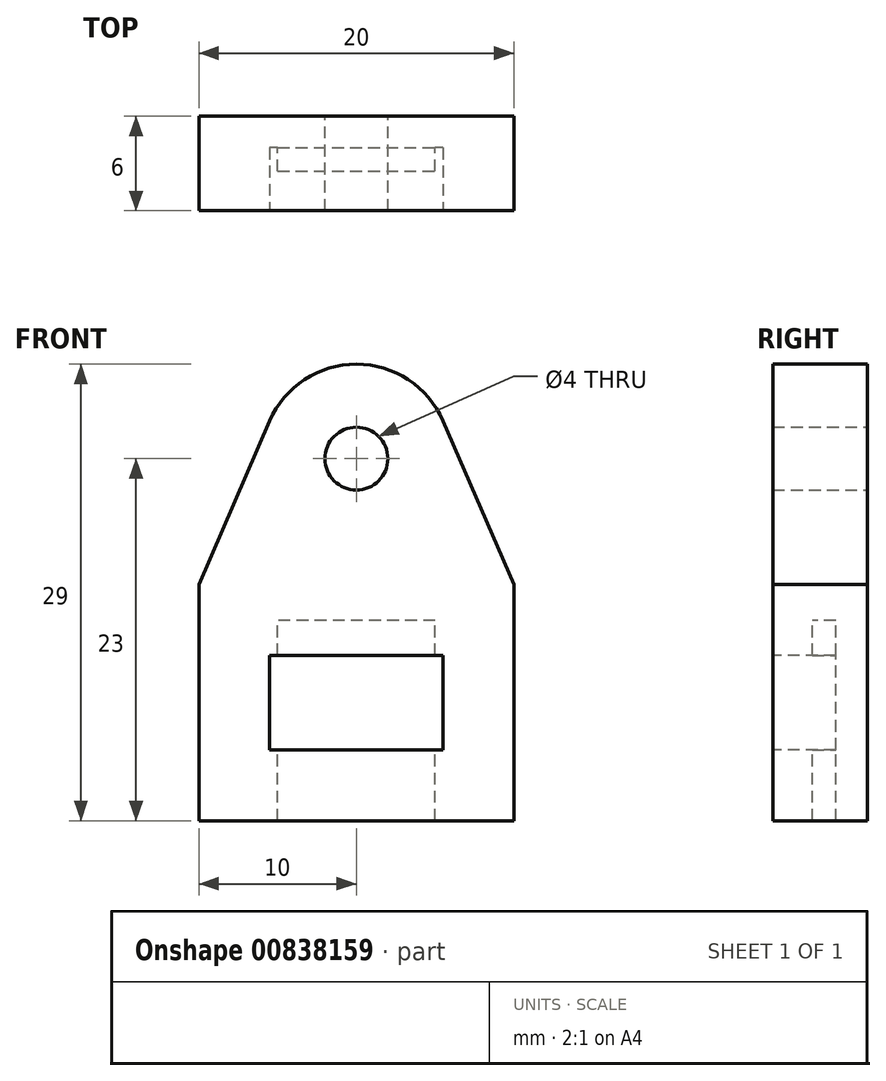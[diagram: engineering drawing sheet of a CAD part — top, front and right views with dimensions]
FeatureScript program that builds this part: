
annotation { "Feature Type Name" : "Feature", "Feature Type Description" : "" }
export const myFeature = defineFeature(function(context is Context, id is Id, definition is map)
    precondition{}
    {
        {
            var Q0;
            Q0=qCreatedBy(makeId("Front.planeOp"),FACE);
            var sketch = newSketch(context, id + "F0", { "sketchPlane" : qUnion([Q0])});
            skLineSegment(sketch, "E0.bottom", {"start": v(0, 0) * mm, "end": v(-20, 0) * mm});
            skLineSegment(sketch, "E0.top", {"start": v(0, 15) * mm, "end": v(-20, 15) * mm});
            skLineSegment(sketch, "E0.left", {"start": v(0, 0) * mm, "end": v(0, 15) * mm});
            skLineSegment(sketch, "E0.right", {"start": v(-20, 0) * mm, "end": v(-20, 15) * mm});
            skLineSegment(sketch, "E1", {"start": v(-10, 43.29) * mm, "end": v(-10, -25.8) * mm, "construction": true});
            skPoint(sketch, "E1.startSnap0", {"position": v(-10, 15) * mm});
            skPoint(sketch, "E1.endSnap0", {"position": v(-10, 0) * mm});
            skPoint(sketch, "E2", {"position": v(-10, 23) * mm});
            skCircle(sketch, "E3", {"center": v(-10, 23) * mm, "radius": 6 * mm});
            skLineSegment(sketch, "E4", {"start": v(-20, 15) * mm, "end": v(-15.5, 25.38) * mm});
            skLineSegment(sketch, "E5", {"start": v(0, 15) * mm, "end": v(-4.5, 25.38) * mm});
            skCircle(sketch, "E6.0", {"center": v(-10, 23) * mm, "radius": 2 * mm});
            skLineSegment(sketch, "E7", {"start": v(-23.7, 7.5) * mm, "end": v(3.2, 7.5) * mm, "construction": true});
            skPoint(sketch, "E7.startSnap0", {"position": v(-20, 7.5) * mm});
            skPoint(sketch, "E8", {"position": v(-10, 7.5) * mm});
            skPoint(sketch, "E8.positionSnap0", {"position": v(-10, 8.74) * mm});
            skLineSegment(sketch, "E9.bottom", {"start": v(-5, 5) * mm, "end": v(-15, 5) * mm});
            skLineSegment(sketch, "E9.top", {"start": v(-5, 10) * mm, "end": v(-15, 10) * mm});
            skLineSegment(sketch, "E9.left", {"start": v(-5, 5) * mm, "end": v(-5, 10) * mm});
            skLineSegment(sketch, "E9.right", {"start": v(-15, 5) * mm, "end": v(-15, 10) * mm});
            skLineSegment(sketch, "E10.bottom", {"start": v(-18, 0) * mm, "end": v(-2, 0) * mm});
            skLineSegment(sketch, "E10.top", {"start": v(-18, 12.72) * mm, "end": v(-2, 12.72) * mm});
            skLineSegment(sketch, "E10.left", {"start": v(-18, 0) * mm, "end": v(-18, 12.72) * mm});
            skLineSegment(sketch, "E10.right", {"start": v(-2, 0) * mm, "end": v(-2, 12.72) * mm});
            skLineSegment(sketch, "E11", {"start": v(-20, 0) * mm, "end": v(-18, 0) * mm});
            skLineSegment(sketch, "E12", {"start": v(-2, 0) * mm, "end": v(0, 0) * mm});
            skSolve(sketch);
        }
        {
            var Q0;
            Q0=makeQuery(id+"F0.imprint","IMPRINT",FACE,{"disambiguationData":[TD([[makeQuery(id+"F0.imprint","IMPRINT",EDGE,{"derivedFrom":sQuery(id+"F0.wireOp",EDGE,"E6.0")}),-1.0]])]});
            var Q1;
            Q1=makeQuery(id+"F0.imprint","IMPRINT",FACE,{"disambiguationData":[TD([[makeQuery(id+"F0.imprint","IMPRINT",EDGE,{"derivedFrom":sQuery(id+"F0.wireOp",EDGE,"E0.top")}),-1.0]])]});
            var Q2;
            Q2=makeQuery(id+"F0.imprint","IMPRINT",FACE,{"disambiguationData":[TD([[makeQuery(id+"F0.imprint","IMPRINT",EDGE,{"derivedFrom":sQuery(id+"F0.wireOp",EDGE,"E0.top")}),1.0]])]});
            var Q3;
            Q3=makeQuery(id+"F0.imprint","IMPRINT",FACE,{"disambiguationData":[TD([[makeQuery(id+"F0.imprint","IMPRINT",EDGE,{"derivedFrom":sQuery(id+"F0.wireOp",EDGE,"E9.bottom")}),1.0]])]});
            var Q4;
            Q4=makeQuery(id+"F0.imprint","IMPRINT",FACE,{"disambiguationData":[TD([[makeQuery(id+"F0.imprint","IMPRINT",EDGE,{"derivedFrom":sQuery(id+"F0.wireOp",EDGE,"E9.bottom")}),-1.0]])]});
            extrude(context, id + "F1", {"entities" : qUnion([Q0, Q1, Q2, Q3, Q4]), "depth" : 6 * mm, "offsetDistance" : 25 * mm});
        }
        {
            var Q0;
            Q0=sQuery(id+"F0.wireOp",EDGE,"E10.top");
            var Q1;
            Q1=qCreatedBy(makeId("Top.planeOp"),FACE);
            cPlane(context, id + "F2", {"entities" : qUnion([Q0, Q1]), "cplaneType" : CPlaneType.LINE_ANGLE, "offset" : 25 * mm, "angle" : 0 * degree, "width" : 150 * mm, "height" : 150 * mm});
        }
        {
            var Q0;
            Q0=qCreatedBy(id+"F2.planeOp",FACE);
            var sketch = newSketch(context, id + "F3", { "sketchPlane" : qUnion([Q0])});
            skPoint(sketch, "E13.0", {"position": v(-10, 0) * mm});
            skLineSegment(sketch, "E14", {"start": v(-10, 6.29) * mm, "end": v(-10, -2.33) * mm, "construction": true});
            skPoint(sketch, "E15", {"position": v(-10, 2.75) * mm});
            skLineSegment(sketch, "E16.bottom", {"start": v(-5, 2) * mm, "end": v(-15, 2) * mm});
            skLineSegment(sketch, "E16.top", {"start": v(-5, 3.5) * mm, "end": v(-15, 3.5) * mm});
            skLineSegment(sketch, "E16.left", {"start": v(-5, 2) * mm, "end": v(-5, 3.5) * mm});
            skLineSegment(sketch, "E16.right", {"start": v(-15, 2) * mm, "end": v(-15, 3.5) * mm});
            skSolve(sketch);
        }
        {
            var Q0;
            Q0=makeQuery(id+"F3.imprint","IMPRINT",FACE,{"disambiguationData":[TD([[makeQuery(id+"F3.imprint","IMPRINT",EDGE,{"derivedFrom":sQuery(id+"F3.wireOp",EDGE,"E16.bottom")}),-1.0]])]});
            extrude(context, id + "F4", {"entities" : qUnion([Q0]), "operationType" : NewBodyOperationType.REMOVE, "depth" : 25 * mm, "offsetDistance" : 25 * mm});
        }
        {
            var Q0;
            Q0=makeQuery(id+"F1.opExtrude","CAP_FACE",FACE,{"disambiguationData":[OSD([sQuery(id+"F0.wireOp",EDGE,"E0.left"),sQuery(id+"F0.wireOp",EDGE,"E0.right"),sQuery(id+"F0.wireOp",EDGE,"E3"),sQuery(id+"F0.wireOp",EDGE,"E4"),sQuery(id+"F0.wireOp",EDGE,"E5"),sQuery(id+"F0.wireOp",EDGE,"E6.0"),sQuery(id+"F0.wireOp",EDGE,"E10.bottom"),sQuery(id+"F0.wireOp",EDGE,"E11"),sQuery(id+"F0.wireOp",EDGE,"E12")])],"isStart":false});
            var sketch = newSketch(context, id + "F5", { "sketchPlane" : qUnion([Q0])});
            skLineSegment(sketch, "E17.0", {"start": v(-15, 5) * mm, "end": v(-15, 10) * mm});
            skLineSegment(sketch, "E17.1", {"start": v(-5, 10) * mm, "end": v(-15, 10) * mm});
            skLineSegment(sketch, "E17.2", {"start": v(-5, 5) * mm, "end": v(-5, 10) * mm});
            skLineSegment(sketch, "E17.3", {"start": v(-5, 5) * mm, "end": v(-15, 5) * mm});
            skLineSegment(sketch, "E18.0", {"start": v(-4.5, 10.5) * mm, "end": v(-15.5, 10.5) * mm});
            skLineSegment(sketch, "E18.1", {"start": v(-4.5, 4.5) * mm, "end": v(-4.5, 10.5) * mm});
            skLineSegment(sketch, "E18.2", {"start": v(-4.5, 4.5) * mm, "end": v(-15.5, 4.5) * mm});
            skLineSegment(sketch, "E18.3", {"start": v(-15.5, 4.5) * mm, "end": v(-15.5, 10.5) * mm});
            skSolve(sketch);
        }
        {
            var Q0;
            Q0=makeQuery(id+"F5.imprint","IMPRINT",FACE,{"disambiguationData":[TD([[makeQuery(id+"F5.imprint","IMPRINT",EDGE,{"derivedFrom":sQuery(id+"F5.wireOp",EDGE,"E17.0")}),-1.0]])]});
            var Q1;
            Q1=makeQuery(id+"F5.imprint","IMPRINT",FACE,{"disambiguationData":[TD([[makeQuery(id+"F5.imprint","IMPRINT",EDGE,{"derivedFrom":sQuery(id+"F5.wireOp",EDGE,"E17.0")}),1.0]])]});
            extrude(context, id + "F6", {"entities" : qUnion([Q0, Q1]), "operationType" : NewBodyOperationType.REMOVE, "oppositeDirection" : true, "depth" : 4 * mm, "offsetDistance" : 25 * mm});
        }
    });
